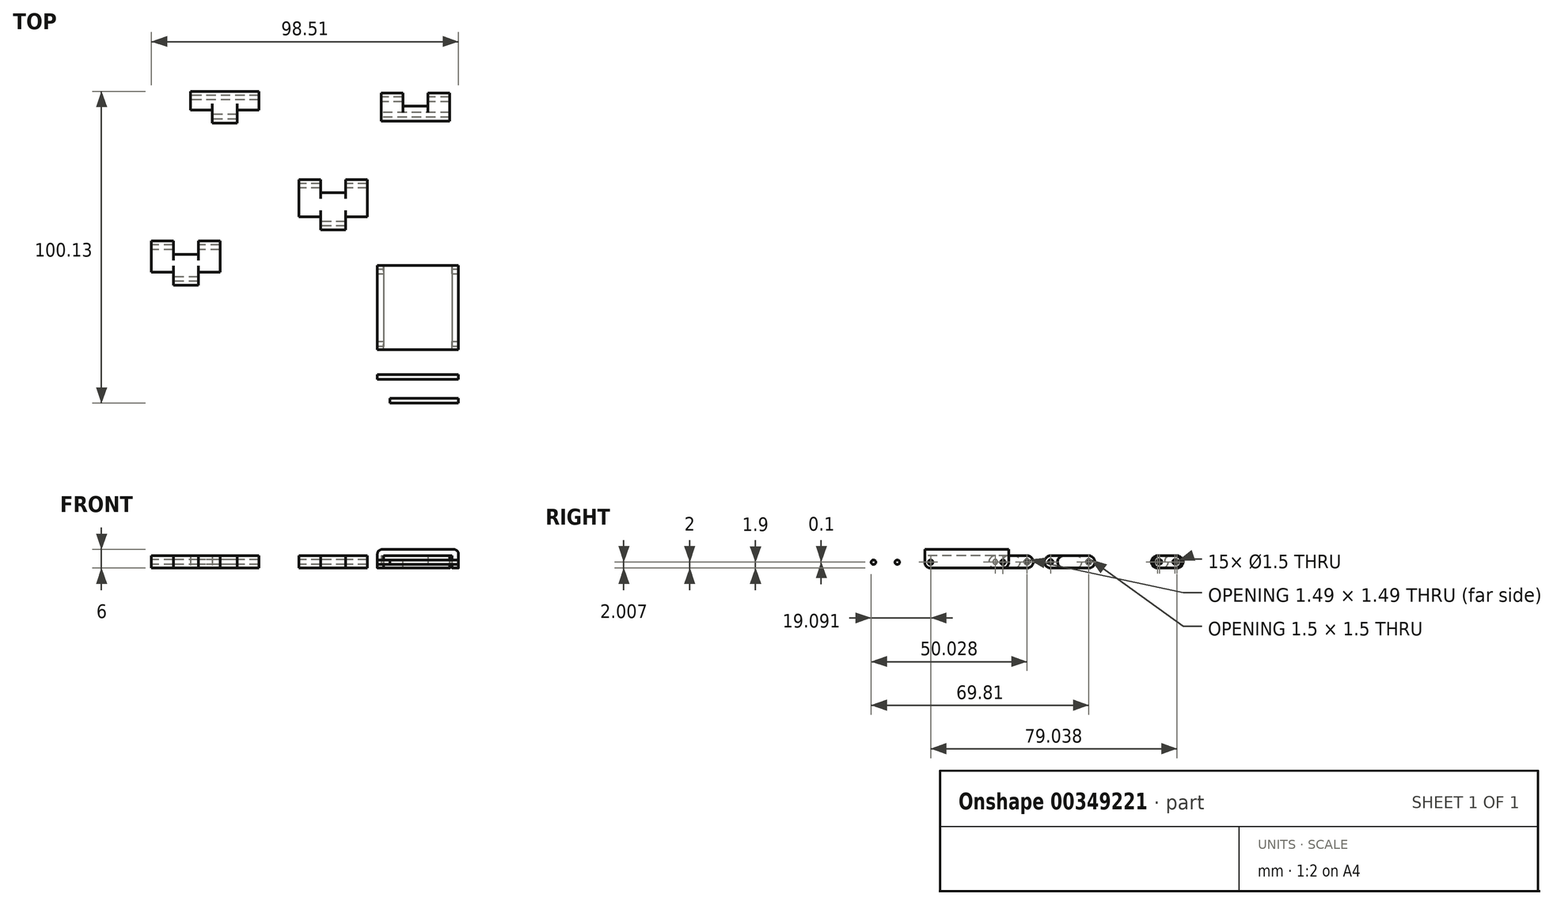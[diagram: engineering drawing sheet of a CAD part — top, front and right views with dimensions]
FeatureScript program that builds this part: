
annotation { "Feature Type Name" : "Feature", "Feature Type Description" : "" }
export const myFeature = defineFeature(function(context is Context, id is Id, definition is map)
    precondition{}
    {
        {
            var Q0;
            Q0=qCreatedBy(makeId("Top.planeOp"),FACE);
            var sketch = newSketch(context, id + "F0", { "sketchPlane" : qUnion([Q0])});
            skPoint(sketch, "E0.middle", {"position": v(0, 0) * mm});
            skLineSegment(sketch, "E1", {"start": v(-11, 6.45) * mm, "end": v(-4, 6.45) * mm});
            skLineSegment(sketch, "E2", {"start": v(-4, 2.25) * mm, "end": v(0, 2.25) * mm});
            skLineSegment(sketch, "E3", {"start": v(-11, -5.55) * mm, "end": v(-4, -5.55) * mm});
            skLineSegment(sketch, "E4", {"start": v(-4, -5.55) * mm, "end": v(-4, -9.75) * mm});
            skLineSegment(sketch, "E5", {"start": v(-4, -9.75) * mm, "end": v(0, -9.75) * mm});
            skLineSegment(sketch, "E6", {"start": v(-11, 6.45) * mm, "end": v(-11, -5.55) * mm});
            skLineSegment(sketch, "E7.MirrorCS", {"start": v(4, 2.25) * mm, "end": v(0, 2.25) * mm});
            skLineSegment(sketch, "E8.MirrorCS", {"start": v(11, 6.45) * mm, "end": v(4, 6.45) * mm});
            skLineSegment(sketch, "E9.MirrorCS", {"start": v(11, -5.55) * mm, "end": v(4, -5.55) * mm});
            skLineSegment(sketch, "E10.MirrorCS", {"start": v(4, -9.75) * mm, "end": v(0, -9.75) * mm});
            skLineSegment(sketch, "E11", {"start": v(11, 6.45) * mm, "end": v(11, -5.55) * mm});
            skPoint(sketch, "E12.middle", {"position": v(26.43, 30.74) * mm});
            skLineSegment(sketch, "E13", {"start": v(15.43, 34.2) * mm, "end": v(22.43, 34.2) * mm});
            skLineSegment(sketch, "E14", {"start": v(22.43, 30) * mm, "end": v(26.43, 30) * mm});
            skLineSegment(sketch, "E15", {"start": v(15.43, 25.2) * mm, "end": v(22.43, 25.2) * mm});
            skLineSegment(sketch, "E16", {"start": v(15.43, 34.2) * mm, "end": v(15.43, 25.2) * mm});
            skLineSegment(sketch, "E17.MirrorCS", {"start": v(30.43, 30) * mm, "end": v(26.43, 30) * mm});
            skLineSegment(sketch, "E18.MirrorCS", {"start": v(37.43, 34.2) * mm, "end": v(30.43, 34.2) * mm});
            skLineSegment(sketch, "E19.MirrorCS", {"start": v(37.43, 25.2) * mm, "end": v(30.43, 25.2) * mm});
            skLineSegment(sketch, "E20", {"start": v(37.43, 34.2) * mm, "end": v(37.43, 25.2) * mm});
            skPoint(sketch, "E21.middle", {"position": v(-34.84, 34.32) * mm});
            skLineSegment(sketch, "E22", {"start": v(-45.84, 34.77) * mm, "end": v(-38.84, 34.77) * mm});
            skLineSegment(sketch, "E23", {"start": v(-45.84, 28.77) * mm, "end": v(-38.84, 28.77) * mm});
            skLineSegment(sketch, "E24", {"start": v(-38.84, 28.77) * mm, "end": v(-38.84, 24.57) * mm});
            skLineSegment(sketch, "E25", {"start": v(-38.84, 24.57) * mm, "end": v(-34.84, 24.57) * mm});
            skLineSegment(sketch, "E26", {"start": v(-45.84, 34.77) * mm, "end": v(-45.84, 28.77) * mm});
            skLineSegment(sketch, "E27.MirrorCS", {"start": v(-23.84, 34.77) * mm, "end": v(-30.84, 34.77) * mm});
            skLineSegment(sketch, "E28.MirrorCS", {"start": v(-23.84, 28.77) * mm, "end": v(-30.84, 28.77) * mm});
            skLineSegment(sketch, "E29.MirrorCS", {"start": v(-30.84, 24.57) * mm, "end": v(-34.84, 24.57) * mm});
            skLineSegment(sketch, "E30", {"start": v(-23.84, 34.77) * mm, "end": v(-23.84, 28.77) * mm});
            skPoint(sketch, "E31.middle", {"position": v(-47.3, -17.79) * mm});
            skLineSegment(sketch, "E32", {"start": v(-58.3, -13.34) * mm, "end": v(-51.3, -13.34) * mm});
            skLineSegment(sketch, "E33", {"start": v(-51.3, -17.54) * mm, "end": v(-47.3, -17.54) * mm});
            skLineSegment(sketch, "E34", {"start": v(-58.3, -23.34) * mm, "end": v(-51.3, -23.34) * mm});
            skLineSegment(sketch, "E35", {"start": v(-51.3, -23.34) * mm, "end": v(-51.3, -27.54) * mm});
            skLineSegment(sketch, "E36", {"start": v(-51.3, -27.54) * mm, "end": v(-47.3, -27.54) * mm});
            skLineSegment(sketch, "E37", {"start": v(-58.3, -13.34) * mm, "end": v(-58.3, -23.34) * mm});
            skLineSegment(sketch, "E38.MirrorCS", {"start": v(-43.3, -17.54) * mm, "end": v(-47.3, -17.54) * mm});
            skLineSegment(sketch, "E39.MirrorCS", {"start": v(-36.3, -13.34) * mm, "end": v(-43.3, -13.34) * mm});
            skLineSegment(sketch, "E40.MirrorCS", {"start": v(-36.3, -23.34) * mm, "end": v(-43.3, -23.34) * mm});
            skLineSegment(sketch, "E41.MirrorCS", {"start": v(-43.3, -27.54) * mm, "end": v(-47.3, -27.54) * mm});
            skLineSegment(sketch, "E42", {"start": v(-36.3, -13.34) * mm, "end": v(-36.3, -23.34) * mm});
            skLineSegment(sketch, "E43", {"start": v(-38.84, 34.77) * mm, "end": v(-30.84, 34.77) * mm});
            skLineSegment(sketch, "E44", {"start": v(22.43, 25.2) * mm, "end": v(30.43, 25.2) * mm});
            skLineSegment(sketch, "E45", {"start": v(-51.3, -13.34) * mm, "end": v(-51.3, -17.54) * mm});
            skLineSegment(sketch, "E46", {"start": v(-43.3, -13.34) * mm, "end": v(-43.3, -17.54) * mm});
            skLineSegment(sketch, "E47", {"start": v(-43.3, -23.34) * mm, "end": v(-43.3, -27.54) * mm});
            skLineSegment(sketch, "E48", {"start": v(-4, 6.45) * mm, "end": v(-4, 2.25) * mm});
            skLineSegment(sketch, "E49", {"start": v(4, 6.45) * mm, "end": v(4, 2.25) * mm});
            skLineSegment(sketch, "E50", {"start": v(4, -5.55) * mm, "end": v(4, -9.75) * mm});
            skLineSegment(sketch, "E51", {"start": v(22.43, 34.2) * mm, "end": v(22.43, 30) * mm});
            skLineSegment(sketch, "E52", {"start": v(30.43, 30) * mm, "end": v(30.43, 34.2) * mm});
            skLineSegment(sketch, "E53", {"start": v(-30.84, 28.77) * mm, "end": v(-30.84, 24.57) * mm});
            skLineSegment(sketch, "E54.bottom", {"start": v(40.22, -21.17) * mm, "end": v(14.22, -21.17) * mm});
            skLineSegment(sketch, "E54.top", {"start": v(40.22, -48.17) * mm, "end": v(14.22, -48.17) * mm});
            skLineSegment(sketch, "E54.left", {"start": v(40.22, -21.17) * mm, "end": v(40.22, -48.17) * mm});
            skLineSegment(sketch, "E54.right", {"start": v(14.22, -21.17) * mm, "end": v(14.22, -48.17) * mm});
            skPoint(sketch, "E54.middle", {"position": v(27.22, -34.67) * mm});
            skLineSegment(sketch, "E55.0", {"start": v(38.22, -18.17) * mm, "end": v(38.22, -48.17) * mm});
            skLineSegment(sketch, "E56.0", {"start": v(16.22, -18.17) * mm, "end": v(16.22, -48.17) * mm});
            skSolve(sketch);
        }
        {
            var Q0;
            Q0=makeQuery(id+"F0.imprint","IMPRINT",FACE,{"disambiguationData":[TD([[makeQuery(id+"F0.imprint","IMPRINT",EDGE,{"derivedFrom":sQuery(id+"F0.wireOp",EDGE,"E22")}),-1.0]])]});
            var Q1;
            Q1=makeQuery(id+"F0.imprint","IMPRINT",FACE,{"disambiguationData":[TD([[makeQuery(id+"F0.imprint","IMPRINT",EDGE,{"derivedFrom":sQuery(id+"F0.wireOp",EDGE,"E13")}),-1.0]])]});
            var Q2;
            Q2=makeQuery(id+"F0.imprint","IMPRINT",FACE,{"disambiguationData":[TD([[makeQuery(id+"F0.imprint","IMPRINT",EDGE,{"derivedFrom":sQuery(id+"F0.wireOp",EDGE,"E1")}),-1.0]])]});
            var Q3;
            Q3=makeQuery(id+"F0.imprint","IMPRINT",FACE,{"disambiguationData":[TD([[makeQuery(id+"F0.imprint","IMPRINT",EDGE,{"derivedFrom":sQuery(id+"F0.wireOp",EDGE,"E32")}),-1.0]])]});
            extrude(context, id + "F1", {"entities" : qUnion([Q0, Q1, Q2, Q3]), "depth" : 4 * mm});
        }
        {
            var Q0;
            Q0=makeQuery(id+"F1.opExtrude","CAP_EDGE",EDGE,{"disambiguationData":[OSD([sQuery(id+"F0.wireOp",EDGE,"E22"),sQuery(id+"F0.wireOp",EDGE,"E27.MirrorCS"),sQuery(id+"F0.wireOp",EDGE,"E43")])],"isStart":false});
            var Q1;
            Q1=makeQuery(id+"F1.opExtrude","CAP_EDGE",EDGE,{"disambiguationData":[OSD([sQuery(id+"F0.wireOp",EDGE,"E23")])],"isStart":false});
            var Q2;
            Q2=makeQuery(id+"F1.opExtrude","CAP_EDGE",EDGE,{"disambiguationData":[OSD([sQuery(id+"F0.wireOp",EDGE,"E23")])],"isStart":true});
            var Q3;
            Q3=makeQuery(id+"F1.opExtrude","CAP_EDGE",EDGE,{"disambiguationData":[OSD([sQuery(id+"F0.wireOp",EDGE,"E28.MirrorCS")])],"isStart":false});
            var Q4;
            Q4=makeQuery(id+"F1.opExtrude","CAP_EDGE",EDGE,{"disambiguationData":[OSD([sQuery(id+"F0.wireOp",EDGE,"E28.MirrorCS")])],"isStart":true});
            var Q5;
            Q5=makeQuery(id+"F1.opExtrude","CAP_EDGE",EDGE,{"disambiguationData":[OSD([sQuery(id+"F0.wireOp",EDGE,"E13")])],"isStart":false});
            var Q6;
            Q6=makeQuery(id+"F1.opExtrude","CAP_EDGE",EDGE,{"disambiguationData":[OSD([sQuery(id+"F0.wireOp",EDGE,"E18.MirrorCS")])],"isStart":false});
            var Q7;
            Q7=makeQuery(id+"F1.opExtrude","CAP_EDGE",EDGE,{"disambiguationData":[OSD([sQuery(id+"F0.wireOp",EDGE,"E15"),sQuery(id+"F0.wireOp",EDGE,"E19.MirrorCS"),sQuery(id+"F0.wireOp",EDGE,"E44")])],"isStart":false});
            var Q8;
            Q8=makeQuery(id+"F1.opExtrude","CAP_EDGE",EDGE,{"disambiguationData":[OSD([sQuery(id+"F0.wireOp",EDGE,"E15"),sQuery(id+"F0.wireOp",EDGE,"E19.MirrorCS"),sQuery(id+"F0.wireOp",EDGE,"E44")])],"isStart":true});
            var Q9;
            Q9=makeQuery(id+"F1.opExtrude","CAP_EDGE",EDGE,{"disambiguationData":[OSD([sQuery(id+"F0.wireOp",EDGE,"E1")])],"isStart":false});
            var Q10;
            Q10=makeQuery(id+"F1.opExtrude","CAP_EDGE",EDGE,{"disambiguationData":[OSD([sQuery(id+"F0.wireOp",EDGE,"E8.MirrorCS")])],"isStart":false});
            var Q11;
            Q11=makeQuery(id+"F1.opExtrude","CAP_EDGE",EDGE,{"disambiguationData":[OSD([sQuery(id+"F0.wireOp",EDGE,"E9.MirrorCS")])],"isStart":false});
            var Q12;
            Q12=makeQuery(id+"F1.opExtrude","CAP_EDGE",EDGE,{"disambiguationData":[OSD([sQuery(id+"F0.wireOp",EDGE,"E3")])],"isStart":false});
            var Q13;
            Q13=makeQuery(id+"F1.opExtrude","CAP_EDGE",EDGE,{"disambiguationData":[OSD([sQuery(id+"F0.wireOp",EDGE,"E32")])],"isStart":false});
            var Q14;
            Q14=makeQuery(id+"F1.opExtrude","CAP_EDGE",EDGE,{"disambiguationData":[OSD([sQuery(id+"F0.wireOp",EDGE,"E39.MirrorCS")])],"isStart":false});
            var Q15;
            Q15=makeQuery(id+"F1.opExtrude","CAP_EDGE",EDGE,{"disambiguationData":[OSD([sQuery(id+"F0.wireOp",EDGE,"E34")])],"isStart":false});
            var Q16;
            Q16=makeQuery(id+"F1.opExtrude","CAP_EDGE",EDGE,{"disambiguationData":[OSD([sQuery(id+"F0.wireOp",EDGE,"E40.MirrorCS")])],"isStart":false});
            var Q17;
            Q17=makeQuery(id+"F1.opExtrude","CAP_EDGE",EDGE,{"disambiguationData":[OSD([sQuery(id+"F0.wireOp",EDGE,"E32")])],"isStart":true});
            var Q18;
            Q18=makeQuery(id+"F1.opExtrude","CAP_EDGE",EDGE,{"disambiguationData":[OSD([sQuery(id+"F0.wireOp",EDGE,"E39.MirrorCS")])],"isStart":true});
            var Q19;
            Q19=makeQuery(id+"F1.opExtrude","CAP_EDGE",EDGE,{"disambiguationData":[OSD([sQuery(id+"F0.wireOp",EDGE,"E40.MirrorCS")])],"isStart":true});
            var Q20;
            Q20=makeQuery(id+"F1.opExtrude","CAP_EDGE",EDGE,{"disambiguationData":[OSD([sQuery(id+"F0.wireOp",EDGE,"E34")])],"isStart":true});
            var Q21;
            Q21=makeQuery(id+"F1.opExtrude","CAP_EDGE",EDGE,{"disambiguationData":[OSD([sQuery(id+"F0.wireOp",EDGE,"E22"),sQuery(id+"F0.wireOp",EDGE,"E27.MirrorCS"),sQuery(id+"F0.wireOp",EDGE,"E43")])],"isStart":true});
            var Q22;
            Q22=makeQuery(id+"F1.opExtrude","CAP_EDGE",EDGE,{"disambiguationData":[OSD([sQuery(id+"F0.wireOp",EDGE,"E13")])],"isStart":true});
            var Q23;
            Q23=makeQuery(id+"F1.opExtrude","CAP_EDGE",EDGE,{"disambiguationData":[OSD([sQuery(id+"F0.wireOp",EDGE,"E18.MirrorCS")])],"isStart":true});
            var Q24;
            Q24=makeQuery(id+"F1.opExtrude","CAP_EDGE",EDGE,{"disambiguationData":[OSD([sQuery(id+"F0.wireOp",EDGE,"E8.MirrorCS")])],"isStart":true});
            var Q25;
            Q25=makeQuery(id+"F1.opExtrude","CAP_EDGE",EDGE,{"disambiguationData":[OSD([sQuery(id+"F0.wireOp",EDGE,"E1")])],"isStart":true});
            var Q26;
            Q26=makeQuery(id+"F1.opExtrude","CAP_EDGE",EDGE,{"disambiguationData":[OSD([sQuery(id+"F0.wireOp",EDGE,"E3")])],"isStart":true});
            var Q27;
            Q27=makeQuery(id+"F1.opExtrude","CAP_EDGE",EDGE,{"disambiguationData":[OSD([sQuery(id+"F0.wireOp",EDGE,"E9.MirrorCS")])],"isStart":true});
            var Q28;
            Q28=makeQuery(id+"F1.opExtrude","CAP_EDGE",EDGE,{"disambiguationData":[OSD([sQuery(id+"F0.wireOp",EDGE,"E36"),sQuery(id+"F0.wireOp",EDGE,"E41.MirrorCS")])],"isStart":true});
            var Q29;
            Q29=makeQuery(id+"F1.opExtrude","CAP_EDGE",EDGE,{"disambiguationData":[OSD([sQuery(id+"F0.wireOp",EDGE,"E33"),sQuery(id+"F0.wireOp",EDGE,"E38.MirrorCS")])],"isStart":true});
            var Q30;
            Q30=makeQuery(id+"F1.opExtrude","CAP_EDGE",EDGE,{"disambiguationData":[OSD([sQuery(id+"F0.wireOp",EDGE,"E25"),sQuery(id+"F0.wireOp",EDGE,"E29.MirrorCS")])],"isStart":true});
            var Q31;
            Q31=makeQuery(id+"F1.opExtrude","CAP_EDGE",EDGE,{"disambiguationData":[OSD([sQuery(id+"F0.wireOp",EDGE,"E2"),sQuery(id+"F0.wireOp",EDGE,"E7.MirrorCS")])],"isStart":true});
            var Q32;
            Q32=makeQuery(id+"F1.opExtrude","CAP_EDGE",EDGE,{"disambiguationData":[OSD([sQuery(id+"F0.wireOp",EDGE,"E5"),sQuery(id+"F0.wireOp",EDGE,"E10.MirrorCS")])],"isStart":true});
            var Q33;
            Q33=makeQuery(id+"F1.opExtrude","CAP_EDGE",EDGE,{"disambiguationData":[OSD([sQuery(id+"F0.wireOp",EDGE,"E14"),sQuery(id+"F0.wireOp",EDGE,"E17.MirrorCS")])],"isStart":true});
            var Q34;
            Q34=makeQuery(id+"F1.opExtrude","CAP_EDGE",EDGE,{"disambiguationData":[OSD([sQuery(id+"F0.wireOp",EDGE,"E25"),sQuery(id+"F0.wireOp",EDGE,"E29.MirrorCS")])],"isStart":false});
            var Q35;
            Q35=makeQuery(id+"F1.opExtrude","CAP_EDGE",EDGE,{"disambiguationData":[OSD([sQuery(id+"F0.wireOp",EDGE,"E14"),sQuery(id+"F0.wireOp",EDGE,"E17.MirrorCS")])],"isStart":false});
            var Q36;
            Q36=makeQuery(id+"F1.opExtrude","CAP_EDGE",EDGE,{"disambiguationData":[OSD([sQuery(id+"F0.wireOp",EDGE,"E2"),sQuery(id+"F0.wireOp",EDGE,"E7.MirrorCS")])],"isStart":false});
            var Q37;
            Q37=makeQuery(id+"F1.opExtrude","CAP_EDGE",EDGE,{"disambiguationData":[OSD([sQuery(id+"F0.wireOp",EDGE,"E5"),sQuery(id+"F0.wireOp",EDGE,"E10.MirrorCS")])],"isStart":false});
            var Q38;
            Q38=makeQuery(id+"F1.opExtrude","CAP_EDGE",EDGE,{"disambiguationData":[OSD([sQuery(id+"F0.wireOp",EDGE,"E36"),sQuery(id+"F0.wireOp",EDGE,"E41.MirrorCS")])],"isStart":false});
            var Q39;
            Q39=makeQuery(id+"F1.opExtrude","CAP_EDGE",EDGE,{"disambiguationData":[OSD([sQuery(id+"F0.wireOp",EDGE,"E33"),sQuery(id+"F0.wireOp",EDGE,"E38.MirrorCS")])],"isStart":false});
            fillet(context, id + "F2", {"entities" : qUnion([Q0, Q1, Q2, Q3, Q4, Q5, Q6, Q7, Q8, Q9, Q10, Q11, Q12, Q13, Q14, Q15, Q16, Q17, Q18, Q19, Q20, Q21, Q22, Q23, Q24, Q25, Q26, Q27, Q28, Q29, Q30, Q31, Q32, Q33, Q34, Q35, Q36, Q37, Q38, Q39]), "radius" : 2 * mm, "tangentPropagation" : true, "allowEdgeOverflow" : false});
        }
        {
            var Q0;
            Q0=makeQuery(id+"F1.opExtrude","SWEPT_FACE",FACE,{"disambiguationData":[OSD([sQuery(id+"F0.wireOp",EDGE,"E26")])]});
            var sketch = newSketch(context, id + "F3", { "sketchPlane" : qUnion([Q0])});
            skCircle(sketch, "E57", {"center": v(-32.77, 2) * mm, "radius": 0.75 * mm});
            skSolve(sketch);
        }
        {
            var Q0;
            Q0=makeQuery(id+"F3.imprint","IMPRINT",FACE,{"disambiguationData":[TD([[makeQuery(id+"F3.imprint","IMPRINT",EDGE,{"derivedFrom":sQuery(id+"F3.wireOp",EDGE,"E57")}),1.0]])]});
            extrude(context, id + "F4", {"entities" : qUnion([Q0]), "operationType" : NewBodyOperationType.REMOVE, "oppositeDirection" : true, "depth" : 22 * mm});
        }
        {
            var Q0;
            Q0=makeQuery(id+"F1.opExtrude","SWEPT_FACE",FACE,{"disambiguationData":[OSD([sQuery(id+"F0.wireOp",EDGE,"E24")])]});
            var sketch = newSketch(context, id + "F5", { "sketchPlane" : qUnion([Q0])});
            skCircle(sketch, "E58", {"center": v(-26.57, 2) * mm, "radius": 0.75 * mm});
            skSolve(sketch);
        }
        {
            var Q0;
            Q0 = qSketchRegion(id + "F5", true);
            extrude(context, id + "F6", {"entities" : qUnion([Q0]), "operationType" : NewBodyOperationType.REMOVE, "oppositeDirection" : true, "depth" : 10 * mm});
        }
        {
            var Q0;
            Q0=makeQuery(id+"F1.opExtrude","SWEPT_FACE",FACE,{"disambiguationData":[OSD([sQuery(id+"F0.wireOp",EDGE,"E16")])]});
            var sketch = newSketch(context, id + "F7", { "sketchPlane" : qUnion([Q0])});
            skCircle(sketch, "E59", {"center": v(-32.2, 2) * mm, "radius": 0.75 * mm});
            skCircle(sketch, "E60", {"center": v(-27.2, 2) * mm, "radius": 0.75 * mm});
            skSolve(sketch);
        }
        {
            var Q0;
            Q0 = qSketchRegion(id + "F7", true);
            extrude(context, id + "F8", {"entities" : qUnion([Q0]), "operationType" : NewBodyOperationType.REMOVE, "oppositeDirection" : true, "depth" : 22 * mm});
        }
        {
            var Q0;
            Q0=makeQuery(id+"F1.opExtrude","SWEPT_FACE",FACE,{"disambiguationData":[OSD([sQuery(id+"F0.wireOp",EDGE,"E6")])]});
            var sketch = newSketch(context, id + "F9", { "sketchPlane" : qUnion([Q0])});
            skCircle(sketch, "E61", {"center": v(-4.45, 2) * mm, "radius": 0.75 * mm});
            skSolve(sketch);
        }
        {
            var Q0;
            Q0 = qSketchRegion(id + "F9", true);
            extrude(context, id + "F10", {"entities" : qUnion([Q0]), "operationType" : NewBodyOperationType.REMOVE, "oppositeDirection" : true, "depth" : 22 * mm});
        }
        {
            var Q0;
            Q0=makeQuery(id+"F1.opExtrude","SWEPT_FACE",FACE,{"disambiguationData":[OSD([sQuery(id+"F0.wireOp",EDGE,"E4")])]});
            var sketch = newSketch(context, id + "F11", { "sketchPlane" : qUnion([Q0])});
            skCircle(sketch, "E62", {"center": v(7.75, 2) * mm, "radius": 0.75 * mm});
            skSolve(sketch);
        }
        {
            var Q0;
            Q0 = qSketchRegion(id + "F11", true);
            extrude(context, id + "F12", {"entities" : qUnion([Q0]), "operationType" : NewBodyOperationType.REMOVE, "oppositeDirection" : true, "depth" : 10 * mm});
        }
        {
            var Q0;
            Q0=makeQuery(id+"F1.opExtrude","SWEPT_FACE",FACE,{"disambiguationData":[OSD([sQuery(id+"F0.wireOp",EDGE,"E37")])]});
            var sketch = newSketch(context, id + "F13", { "sketchPlane" : qUnion([Q0])});
            skCircle(sketch, "E63", {"center": v(15.34, 2) * mm, "radius": 0.75 * mm});
            skSolve(sketch);
        }
        {
            var Q0;
            Q0=makeQuery(id+"F13.imprint","IMPRINT",FACE,{"disambiguationData":[TD([[makeQuery(id+"F13.imprint","IMPRINT",EDGE,{"derivedFrom":sQuery(id+"F13.wireOp",EDGE,"E63")}),1.0]])]});
            extrude(context, id + "F14", {"entities" : qUnion([Q0]), "operationType" : NewBodyOperationType.REMOVE, "oppositeDirection" : true, "depth" : 22 * mm});
        }
        {
            var Q0;
            Q0=makeQuery(id+"F1.opExtrude","SWEPT_FACE",FACE,{"disambiguationData":[OSD([sQuery(id+"F0.wireOp",EDGE,"E35")])]});
            var sketch = newSketch(context, id + "F15", { "sketchPlane" : qUnion([Q0])});
            skCircle(sketch, "E64", {"center": v(25.54, 2) * mm, "radius": 0.75 * mm});
            skSolve(sketch);
        }
        {
            var Q0;
            Q0 = qSketchRegion(id + "F15", true);
            extrude(context, id + "F16", {"entities" : qUnion([Q0]), "operationType" : NewBodyOperationType.REMOVE, "oppositeDirection" : true, "depth" : 10 * mm});
        }
        {
            var Q0;
            {var subQ0=sQuery(id+"F0.wireOp",EDGE,"E54.right");Q0=makeQuery(id+"F0.imprint","IMPRINT",FACE,{"disambiguationData":[TD([[makeQuery(id+"F0.imprint","IMPRINT",EDGE,{"derivedFrom":subQ0}),1.0]])]});}
            var Q1;
            {var subQ0=sQuery(id+"F0.wireOp",EDGE,"E55.0");Q1=makeQuery(id+"F0.imprint","IMPRINT",FACE,{"disambiguationData":[TD([[makeQuery(id+"F0.imprint","IMPRINT",EDGE,{"derivedFrom":subQ0}),-1.0]])]});}
            var Q2;
            {var subQ0=sQuery(id+"F0.wireOp",EDGE,"E54.left");Q2=makeQuery(id+"F0.imprint","IMPRINT",FACE,{"disambiguationData":[TD([[makeQuery(id+"F0.imprint","IMPRINT",EDGE,{"derivedFrom":subQ0}),-1.0]])]});}
            extrude(context, id + "F17", {"entities" : qUnion([Q0, Q1, Q2]), "depth" : 6 * mm});
        }
        {
            var Q0;
            {var subQ0=sQuery(id+"F0.wireOp",EDGE,"E55.0");Q0=makeQuery(id+"F0.imprint","IMPRINT",FACE,{"disambiguationData":[TD([[makeQuery(id+"F0.imprint","IMPRINT",EDGE,{"derivedFrom":subQ0}),-1.0]])]});}
            extrude(context, id + "F18", {"entities" : qUnion([Q0]), "operationType" : NewBodyOperationType.REMOVE, "depth" : 4 * mm});
        }
        {
            var Q0;
            {var subQ0=sQuery(id+"F0.wireOp",EDGE,"E54.left");var subQ1=sQuery(id+"F0.wireOp",EDGE,"E54.top");Q0=makeQuery(id+"F18.boolean.opBoolean","SPLIT",EDGE,{"disambiguationData":[TD([makeQuery(id+"F17.opExtrude","SWEPT_FACE",FACE,{"disambiguationData":[OSD([subQ0])]})])],"derivedFrom":makeQuery(id+"F17.opExtrude","CAP_EDGE",EDGE,{"disambiguationData":[OSD([subQ1])],"isStart":true})});}
            var Q1;
            {var subQ0=sQuery(id+"F0.wireOp",EDGE,"E54.bottom");var subQ1=sQuery(id+"F0.wireOp",EDGE,"E54.left");Q1=makeQuery(id+"F18.boolean.opBoolean","SPLIT",EDGE,{"disambiguationData":[TD([makeQuery(id+"F17.opExtrude","SWEPT_FACE",FACE,{"disambiguationData":[OSD([subQ1])]})])],"derivedFrom":makeQuery(id+"F17.opExtrude","CAP_EDGE",EDGE,{"disambiguationData":[OSD([subQ0])],"isStart":true})});}
            var Q2;
            {var subQ0=sQuery(id+"F0.wireOp",EDGE,"E54.right");var subQ1=sQuery(id+"F0.wireOp",EDGE,"E54.top");Q2=makeQuery(id+"F18.boolean.opBoolean","SPLIT",EDGE,{"disambiguationData":[TD([makeQuery(id+"F17.opExtrude","SWEPT_FACE",FACE,{"disambiguationData":[OSD([subQ0])]})])],"derivedFrom":makeQuery(id+"F17.opExtrude","CAP_EDGE",EDGE,{"disambiguationData":[OSD([subQ1])],"isStart":true})});}
            var Q3;
            {var subQ0=sQuery(id+"F0.wireOp",EDGE,"E54.bottom");var subQ1=sQuery(id+"F0.wireOp",EDGE,"E54.right");Q3=makeQuery(id+"F18.boolean.opBoolean","SPLIT",EDGE,{"disambiguationData":[TD([makeQuery(id+"F17.opExtrude","SWEPT_FACE",FACE,{"disambiguationData":[OSD([subQ1])]})])],"derivedFrom":makeQuery(id+"F17.opExtrude","CAP_EDGE",EDGE,{"disambiguationData":[OSD([subQ0])],"isStart":true})});}
            fillet(context, id + "F19", {"entities" : qUnion([Q0, Q1, Q2, Q3]), "radius" : 1.9 * mm, "tangentPropagation" : true, "allowEdgeOverflow" : false});
        }
        {
            var Q0;
            Q0=makeQuery(id+"F17.opExtrude","SWEPT_FACE",FACE,{"disambiguationData":[OSD([sQuery(id+"F0.wireOp",EDGE,"E54.left")])]});
            var sketch = newSketch(context, id + "F20", { "sketchPlane" : qUnion([Q0])});
            skCircle(sketch, "E65", {"center": v(-46.27, 1.9) * mm, "radius": 0.75 * mm});
            skCircle(sketch, "E66", {"center": v(-23.07, 1.9) * mm, "radius": 0.75 * mm});
            skCircle(sketch, "E67", {"center": v(-56.97, 1.9) * mm, "radius": 0.75 * mm});
            skCircle(sketch, "E68", {"center": v(-64.6, 1.9) * mm, "radius": 0.75 * mm});
            skSolve(sketch);
        }
        {
            var Q0;
            Q0=makeQuery(id+"F20.imprint","IMPRINT",FACE,{"disambiguationData":[TD([[makeQuery(id+"F20.imprint","IMPRINT",EDGE,{"derivedFrom":sQuery(id+"F20.wireOp",EDGE,"E65")}),1.0]])]});
            var Q1;
            Q1=makeQuery(id+"F20.imprint","IMPRINT",FACE,{"disambiguationData":[TD([[makeQuery(id+"F20.imprint","IMPRINT",EDGE,{"derivedFrom":sQuery(id+"F20.wireOp",EDGE,"E66")}),1.0]])]});
            extrude(context, id + "F21", {"entities" : qUnion([Q0, Q1]), "operationType" : NewBodyOperationType.REMOVE, "oppositeDirection" : true, "depth" : 26 * mm});
        }
        {
            var Q0;
            Q0=makeQuery(id+"F20.imprint","IMPRINT",FACE,{"disambiguationData":[TD([[makeQuery(id+"F20.imprint","IMPRINT",EDGE,{"derivedFrom":sQuery(id+"F20.wireOp",EDGE,"E67")}),1.0]])]});
            extrude(context, id + "F22", {"entities" : qUnion([Q0]), "oppositeDirection" : true, "depth" : 26 * mm});
        }
        {
            var Q0;
            Q0=makeQuery(id+"F20.imprint","IMPRINT",FACE,{"disambiguationData":[TD([[makeQuery(id+"F20.imprint","IMPRINT",EDGE,{"derivedFrom":sQuery(id+"F20.wireOp",EDGE,"E68")}),1.0]])]});
            extrude(context, id + "F23", {"entities" : qUnion([Q0]), "oppositeDirection" : true, "depth" : 22 * mm});
        }
        {
            var Q0;
            Q0=makeQuery(id+"F17.opExtrude","CAP_EDGE",EDGE,{"disambiguationData":[OSD([sQuery(id+"F0.wireOp",EDGE,"E54.left")])],"isStart":false});
            var Q1;
            Q1=makeQuery(id+"F17.opExtrude","CAP_EDGE",EDGE,{"disambiguationData":[OSD([sQuery(id+"F0.wireOp",EDGE,"E54.right")])],"isStart":false});
            fillet(context, id + "F24", {"entities" : qUnion([Q0, Q1]), "radius" : 1.5 * mm, "tangentPropagation" : true, "allowEdgeOverflow" : false});
        }
    });
